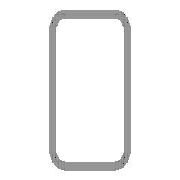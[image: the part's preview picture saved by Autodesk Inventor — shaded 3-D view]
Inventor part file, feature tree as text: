
AUTODESK INVENTOR PART (.ipt)
format: ipt  version: 2025.3 (Build 293356030, 356C)  size: 149,504 bytes
history: native  units: mm (DEFAULTED — no unit token found)
features: other x4, plane x3, split x2, sketch x1
ambient origin geometry x8: Origin, YZ Plane, XZ Plane, XY Plane, X Axis, Y Axis, Z Axis, Center Point
bodies: Solid1 (feature_tree), Body (feature_tree)
feature tree (10):
  parser-record x1  (decoder bookkeeping rows leaked as tree rows — omitted from the tree; the rows remain in map.json)
  other  "Driven Length"
  other  "Start Plane"
  other  "End Plane"
  plane  "Work Plane4"
  split  "Split1"
  plane  "Work Plane5"
  split  "Split2"
  sketch  "Sketch3"  dims[d3=2924.995667mm d4=0.0mm d7=4.0mm d9=20.0mm d11=40.0mm d12=2.0mm d13=73.137085mm d14=2998.132752mm d15=10.0mm d16=20.0mm d17=90.0deg d18=2924.995667mm]
  plane  "Work Plane3"
